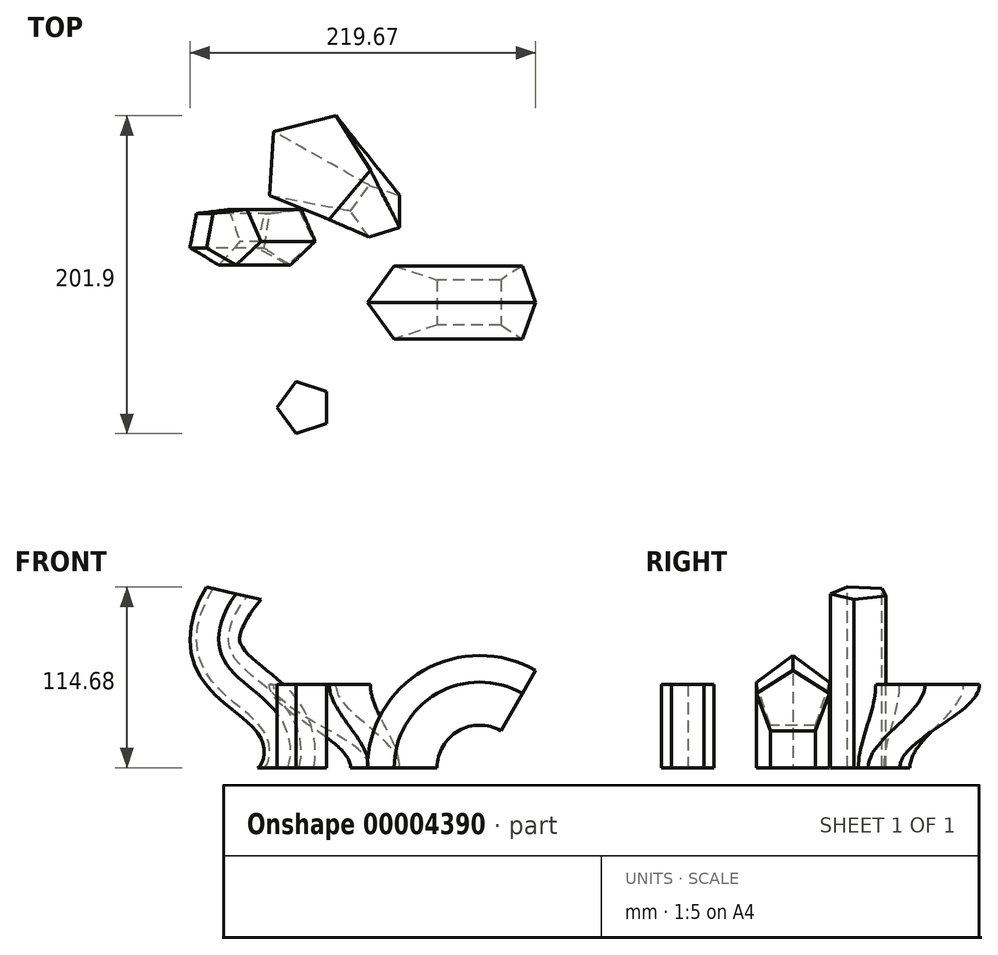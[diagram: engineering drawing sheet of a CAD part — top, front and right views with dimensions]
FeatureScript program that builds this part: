
annotation { "Feature Type Name" : "Feature", "Feature Type Description" : "" }
export const myFeature = defineFeature(function(context is Context, id is Id, definition is map)
    precondition{}
    {
        {
            var Q0;
            Q0=qCreatedBy(makeId("Top.planeOp"),FACE);
            var sketch = newSketch(context, id + "F0", { "sketchPlane" : qUnion([Q0])});
            skCircle(sketch, "E0.cCircle", {"center": v(-115.09, -42.53) * mm, "radius": 19.79 * mm, "construction": true});
            skLineSegment(sketch, "E0.0", {"start": v(-95.3, -28.16) * mm, "end": v(-95.3, -56.9) * mm});
            skLineSegment(sketch, "E0.1", {"start": v(-95.3, -56.9) * mm, "end": v(-122.65, -65.8) * mm});
            skLineSegment(sketch, "E0.2", {"start": v(-122.65, -65.8) * mm, "end": v(-139.55, -42.53) * mm});
            skLineSegment(sketch, "E0.3", {"start": v(-139.55, -42.53) * mm, "end": v(-122.65, -19.27) * mm});
            skLineSegment(sketch, "E0.4", {"start": v(-122.65, -19.27) * mm, "end": v(-95.3, -28.16) * mm});
            skPoint(sketch, "E0.0.midPoint", {"position": v(-95.3, -42.53) * mm});
            skCircle(sketch, "E1.cCircle", {"center": v(-179.66, -109.3) * mm, "radius": 14.1 * mm, "construction": true});
            skLineSegment(sketch, "E1.0", {"start": v(-165.55, -99.06) * mm, "end": v(-165.55, -119.55) * mm});
            skLineSegment(sketch, "E1.1", {"start": v(-165.55, -119.55) * mm, "end": v(-185.04, -125.88) * mm});
            skLineSegment(sketch, "E1.2", {"start": v(-185.04, -125.88) * mm, "end": v(-197.09, -109.3) * mm});
            skLineSegment(sketch, "E1.3", {"start": v(-197.09, -109.3) * mm, "end": v(-185.04, -92.73) * mm});
            skLineSegment(sketch, "E1.4", {"start": v(-185.04, -92.73) * mm, "end": v(-165.55, -99.06) * mm});
            skPoint(sketch, "E1.0.midPoint", {"position": v(-165.55, -109.3) * mm});
            skCircle(sketch, "E2.cCircle", {"center": v(-192.32, 0) * mm, "radius": 15.27 * mm, "construction": true});
            skLineSegment(sketch, "E2.0", {"start": v(-173.81, -3.75) * mm, "end": v(-190.17, -18.76) * mm});
            skLineSegment(sketch, "E2.1", {"start": v(-190.17, -18.76) * mm, "end": v(-209.5, -7.84) * mm});
            skLineSegment(sketch, "E2.2", {"start": v(-209.5, -7.84) * mm, "end": v(-205.08, 13.91) * mm});
            skLineSegment(sketch, "E2.3", {"start": v(-205.08, 13.91) * mm, "end": v(-183.03, 16.44) * mm});
            skLineSegment(sketch, "E2.4", {"start": v(-183.03, 16.44) * mm, "end": v(-173.81, -3.75) * mm});
            skPoint(sketch, "E2.0.midPoint", {"position": v(-182, -11.26) * mm});
            skLineSegment(sketch, "E3", {"start": v(-68.32, -81.48) * mm, "end": v(-68.32, 1.53) * mm});
            skCircle(sketch, "E4.cCircle", {"center": v(-133.1, 15.38) * mm, "radius": 13.94 * mm, "construction": true});
            skLineSegment(sketch, "E4.0", {"start": v(-138.32, 31.8) * mm, "end": v(-119.1, 25.43) * mm});
            skLineSegment(sketch, "E4.1", {"start": v(-119.1, 25.43) * mm, "end": v(-119.21, 5.18) * mm});
            skLineSegment(sketch, "E4.2", {"start": v(-119.21, 5.18) * mm, "end": v(-138.5, -0.97) * mm});
            skLineSegment(sketch, "E4.3", {"start": v(-138.5, -0.97) * mm, "end": v(-150.32, 15.48) * mm});
            skLineSegment(sketch, "E4.4", {"start": v(-150.32, 15.48) * mm, "end": v(-138.32, 31.8) * mm});
            skPoint(sketch, "E4.0.midPoint", {"position": v(-128.71, 28.61) * mm});
            skSolve(sketch);
        }
        {
            var Q0;
            Q0=makeQuery(id+"F0.imprint","IMPRINT",FACE,{"disambiguationData":[TD([[makeQuery(id+"F0.imprint","IMPRINT",EDGE,{"derivedFrom":sQuery(id+"F0.wireOp",EDGE,"E1.0")}),-1.0]])]});
            extrude(context, id + "F1", {"entities" : qUnion([Q0]), "depth" : 52.93 * mm});
        }
        {
            var Q0;
            Q0=makeQuery(id+"F0.imprint","IMPRINT",FACE,{"disambiguationData":[TD([[makeQuery(id+"F0.imprint","IMPRINT",EDGE,{"derivedFrom":sQuery(id+"F0.wireOp",EDGE,"E0.0")}),-1.0]])]});
            var Q1;
            Q1=sQuery(id+"F0.wireOp",EDGE,"E3");
            revolve(context, id + "F2", {"entities" : qUnion([Q0]), "axis" : qUnion([Q1]), "revolveType" : RevolveType.ONE_DIRECTION, "angle" : 120 * degree});
        }
        {
            var Q0;
            Q0=qCreatedBy(makeId("Front.planeOp"),FACE);
            var sketch = newSketch(context, id + "F3", { "sketchPlane" : qUnion([Q0])});
            skPoint(sketch, "E5.0", {"position": v(-192.32, 0) * mm});
            skFitSpline(sketch, "E6", {"points": [v(-192.32, 0) * mm, v(-198.2, 32.84) * mm, v(-231.13, 65.3) * mm, v(-225.1, 110.96) * mm], "startDerivative": vector(40.8, 98.7) * mm, "endDerivative": vector(110.69, 158.35) * mm});
            skSolve(sketch);
        }
        {
            var Q0;
            Q0=makeQuery(id+"F0.imprint","IMPRINT",FACE,{"disambiguationData":[TD([[makeQuery(id+"F0.imprint","IMPRINT",EDGE,{"derivedFrom":sQuery(id+"F0.wireOp",EDGE,"E2.0")}),-1.0]])]});
            var Q1;
            Q1=sQuery(id+"F3.wireOp",EDGE,"E6");
            sweep(context, id + "F4", {"profiles" : qUnion([Q0]), "path" : qUnion([Q1])});
        }
        {
            var Q0;
            Q0=makeQuery(id+"F1.opExtrude","CAP_FACE",FACE,{"disambiguationData":[OSD([sQuery(id+"F0.wireOp",EDGE,"E1.0"),sQuery(id+"F0.wireOp",EDGE,"E1.1"),sQuery(id+"F0.wireOp",EDGE,"E1.2"),sQuery(id+"F0.wireOp",EDGE,"E1.3"),sQuery(id+"F0.wireOp",EDGE,"E1.4")])],"isStart":false});
            var sketch = newSketch(context, id + "F5", { "sketchPlane" : qUnion([Q0])});
            skCircle(sketch, "E7.cCircle", {"center": v(-172.39, 43.75) * mm, "radius": 28.1 * mm, "construction": true});
            skLineSegment(sketch, "E7.0", {"start": v(-199.1, 65.97) * mm, "end": v(-159.51, 76.02) * mm});
            skLineSegment(sketch, "E7.1", {"start": v(-159.51, 76.02) * mm, "end": v(-137.72, 41.48) * mm});
            skLineSegment(sketch, "E7.2", {"start": v(-137.72, 41.48) * mm, "end": v(-163.83, 10.07) * mm});
            skLineSegment(sketch, "E7.3", {"start": v(-163.83, 10.07) * mm, "end": v(-201.77, 25.2) * mm});
            skLineSegment(sketch, "E7.4", {"start": v(-201.77, 25.2) * mm, "end": v(-199.1, 65.97) * mm});
            skPoint(sketch, "E7.0.midPoint", {"position": v(-179.3, 71) * mm});
            skSolve(sketch);
        }
        {
            var Q0;
            Q0=makeQuery(id+"F0.imprint","IMPRINT",FACE,{"disambiguationData":[TD([[makeQuery(id+"F0.imprint","IMPRINT",EDGE,{"derivedFrom":sQuery(id+"F0.wireOp",EDGE,"E4.0")}),-1.0]])]});
            var Q1;
            Q1=makeQuery(id+"F5.imprint","IMPRINT",FACE,{"disambiguationData":[TD([[makeQuery(id+"F5.imprint","IMPRINT",EDGE,{"derivedFrom":sQuery(id+"F5.wireOp",EDGE,"E7.0")}),-1.0]])]});
            loft(context, id + "F6", {"operationType" : NewBodyOperationType.ADD, "sheetProfilesArray" : [{ "sheetProfileEntities" : qUnion([Q0]) }, { "sheetProfileEntities" : qUnion([Q1]) }], "startCondition" : LoftEndDerivativeType.NORMAL_TO_PROFILE, "startMagnitude" : 1, "endCondition" : LoftEndDerivativeType.NORMAL_TO_PROFILE, "endMagnitude" : 1});
        }
    });
